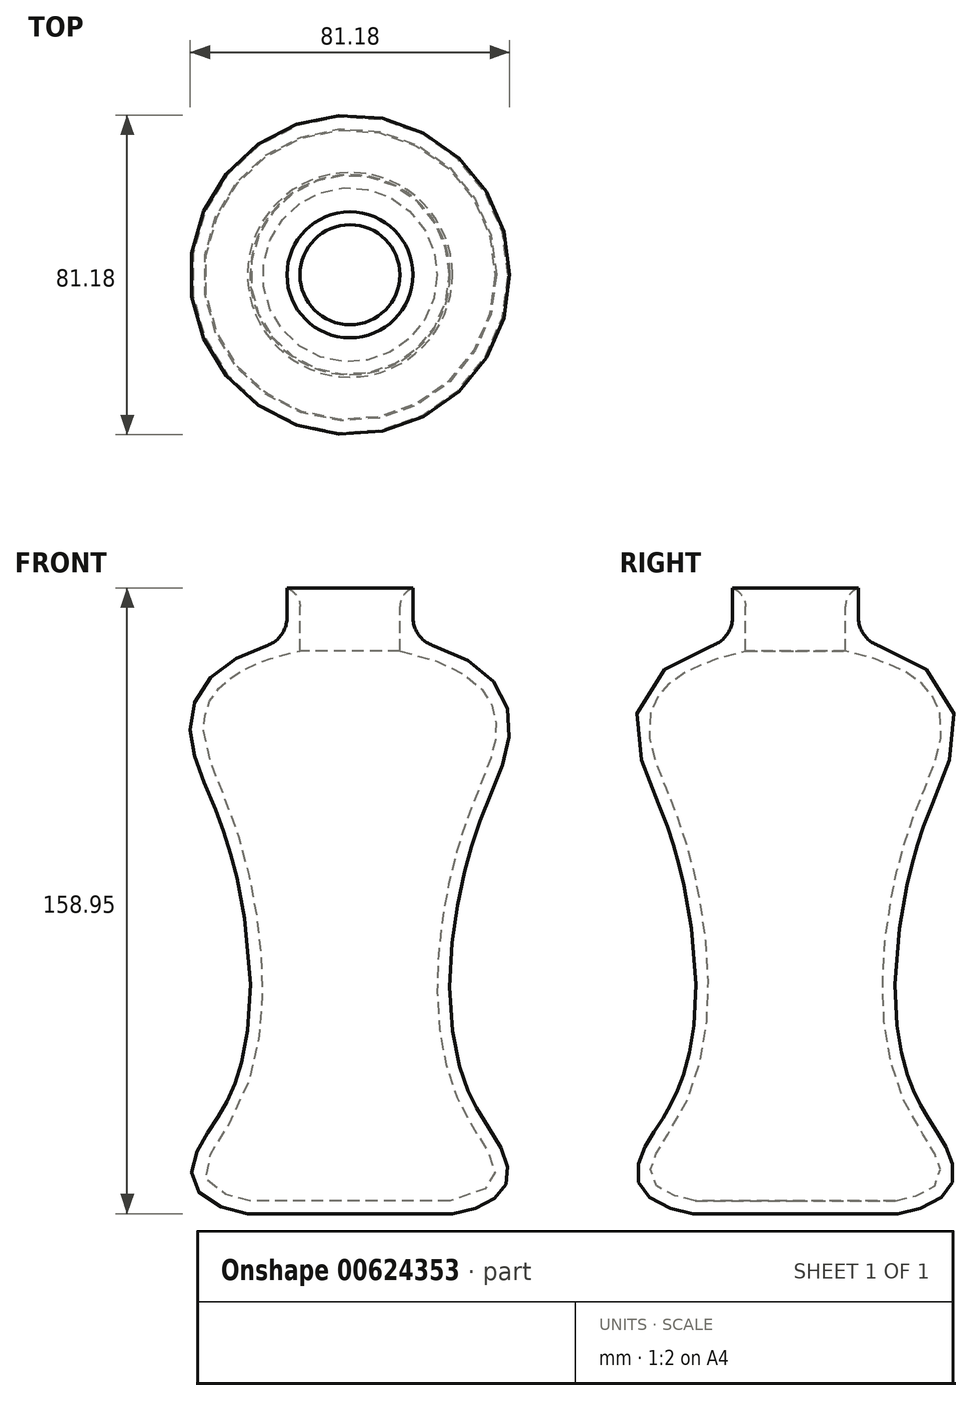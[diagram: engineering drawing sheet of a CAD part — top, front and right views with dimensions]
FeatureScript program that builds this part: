
annotation { "Feature Type Name" : "Feature", "Feature Type Description" : "" }
export const myFeature = defineFeature(function(context is Context, id is Id, definition is map)
    precondition{}
    {
        {
            var Q0;
            Q0=qCreatedBy(makeId("Right.planeOp"),FACE);
            var sketch = newSketch(context, id + "F0", { "sketchPlane" : qUnion([Q0])});
            skLineSegment(sketch, "E0", {"start": v(0, 0) * mm, "end": v(25.4, 0) * mm});
            skLineSegment(sketch, "E1", {"start": v(12.7, 152.4) * mm, "end": v(12.7, 139.7) * mm});
            skFitSpline(sketch, "E2", {"points": [v(12.7, 139.7) * mm, v(37.17, 119.97) * mm, v(28.4, 93.08) * mm, v(28.4, 23.64) * mm, v(25.4, 0) * mm], "startDerivative": vector(251.9, -52.1) * mm, "endDerivative": vector(-296.34, -55.61) * mm});
            skFitSpline(sketch, "E3.0", {"points": [v(13.37, 142.93) * mm, v(16.1, 142.37) * mm, v(21.03, 141.1) * mm, v(27.1, 138.74) * mm, v(31.94, 135.98) * mm, v(35.67, 132.79) * mm, v(38.32, 129.22) * mm, v(39.92, 125.4) * mm, v(40.55, 121.54) * mm, v(40.44, 117.8) * mm, v(39.75, 114.17) * mm, v(38.65, 110.58) * mm, v(37.26, 106.93) * mm, v(35.68, 103.1) * mm, v(34.01, 98.98) * mm, v(32.6, 95.23) * mm, v(31.5, 92) * mm, v(30.7, 89.43) * mm, v(29.94, 86.73) * mm, v(28.97, 82.97) * mm, v(27.86, 78) * mm, v(26.76, 71.74) * mm, v(25.95, 65.26) * mm, v(25.33, 56.48) * mm, v(25.49, 47.7) * mm, v(26.63, 39.32) * mm, v(27.78, 34.34) * mm, v(29, 30.57) * mm, v(29.87, 28.3) * mm, v(30.65, 26.56) * mm, v(31.26, 25.28) * mm, v(31.93, 24.04) * mm, v(32.87, 22.38) * mm, v(34.12, 20.35) * mm, v(35.65, 17.96) * mm, v(37.12, 15.63) * mm, v(38.44, 13.32) * mm, v(39.34, 11.36) * mm, v(39.86, 9.7) * mm, v(40.12, 8.4) * mm, v(40.2, 7.04) * mm, v(40.05, 5.61) * mm, v(39.62, 4.19) * mm, v(38.9, 2.85) * mm, v(37.94, 1.67) * mm, v(36.78, 0.65) * mm, v(35.45, -0.22) * mm, v(33.47, -1.23) * mm, v(30.55, -2.27) * mm, v(27.63, -2.94) * mm, v(26, -3.25) * mm]});
            skLineSegment(sketch, "E3.1", {"start": v(16, 155.7) * mm, "end": v(16, 142.35) * mm});
            skLineSegment(sketch, "E3.2", {"start": v(12.7, 155.7) * mm, "end": v(16, 155.7) * mm});
            skLineSegment(sketch, "E4", {"start": v(0, 0) * mm, "end": v(0, -3.25) * mm});
            skLineSegment(sketch, "E5", {"start": v(0, -3.25) * mm, "end": v(26, -3.25) * mm});
            skLineSegment(sketch, "E6", {"start": v(12.7, 152.4) * mm, "end": v(12.7, 155.7) * mm});
            skSolve(sketch);
        }
        {
            var Q0;
            Q0 = qSketchRegion(id + "F0", true);
            var Q1;
            Q1=sQuery(id+"F0.wireOp",EDGE,"E4");
            revolve(context, id + "F1", {"entities" : qUnion([Q0]), "axis" : qUnion([Q1]), "revolveType" : RevolveType.FULL});
        }
        {
            var Q0;
            Q0=makeQuery(id+"F1.opRevolve","SWEPT_EDGE",EDGE,{"disambiguationData":[OSD([sQuery(id+"F0.wireOp",EDGE,"E3.2"),sQuery(id+"F0.wireOp",EDGE,"E6")])]});
            fillet(context, id + "F2", {"entities" : qUnion([Q0]), "radius" : 5.08 * mm, "tangentPropagation" : true, "allowEdgeOverflow" : false});
        }
        {
            var Q0;
            Q0=makeQuery(id+"F1.opRevolve","SWEPT_EDGE",EDGE,{"disambiguationData":[OSD([sQuery(id+"F0.wireOp",EDGE,"E3.0"),sQuery(id+"F0.wireOp",EDGE,"E3.1")])]});
            fillet(context, id + "F3", {"entities" : qUnion([Q0]), "radius" : 7.62 * mm, "tangentPropagation" : true, "allowEdgeOverflow" : false});
        }
    });
